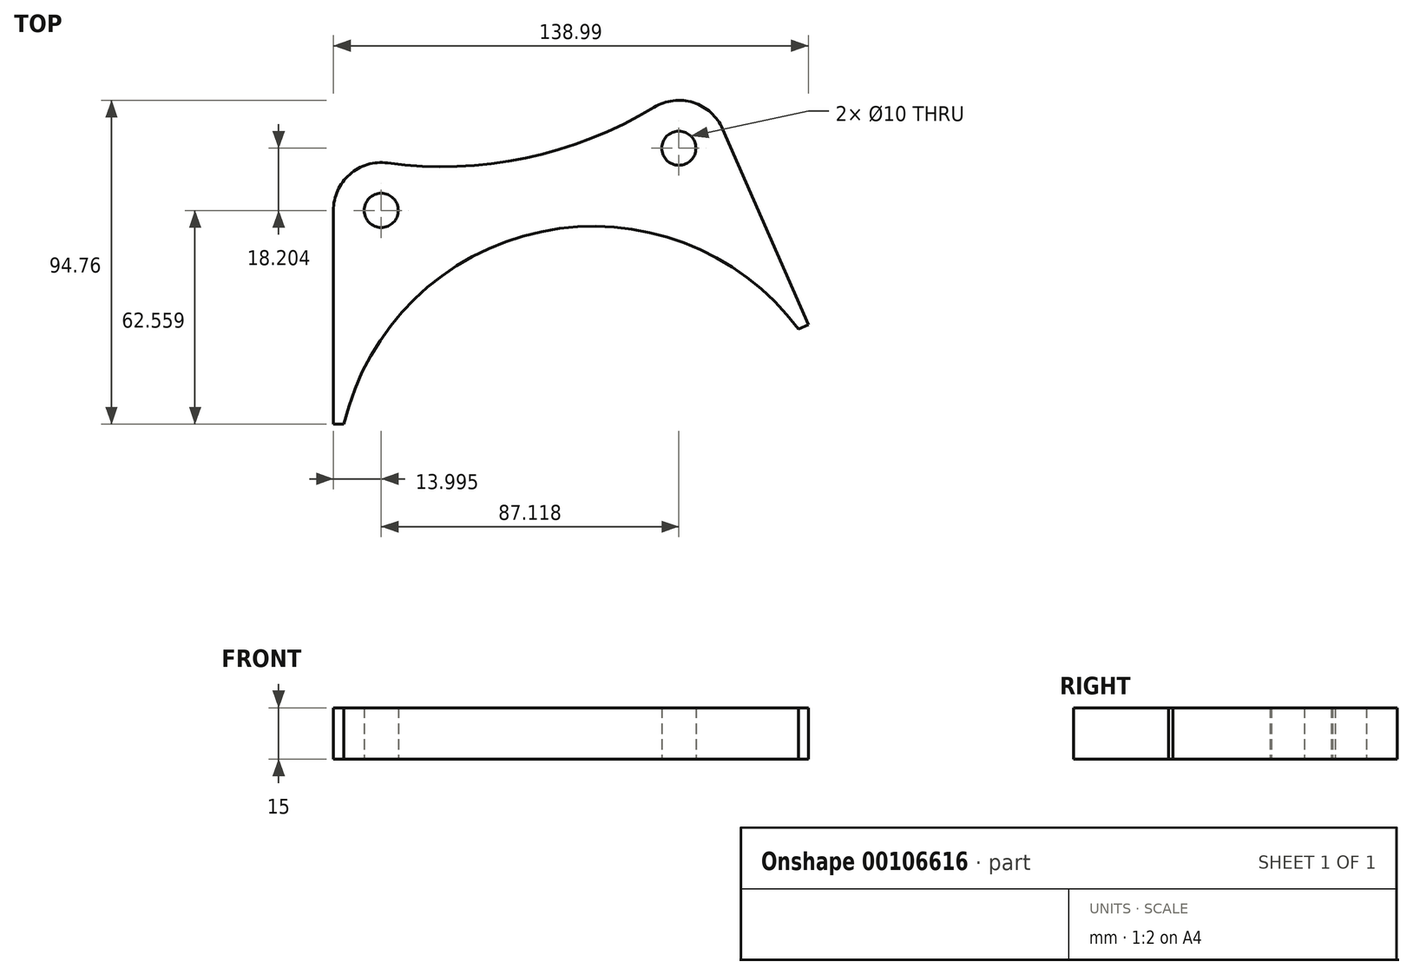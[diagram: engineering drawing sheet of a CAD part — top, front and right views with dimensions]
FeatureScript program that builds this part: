
annotation { "Feature Type Name" : "Feature", "Feature Type Description" : "" }
export const myFeature = defineFeature(function(context is Context, id is Id, definition is map)
    precondition{}
    {
        {
            var Q0;
            Q0=qCreatedBy(makeId("Top.planeOp"),FACE);
            var sketch = newSketch(context, id + "F0", { "sketchPlane" : qUnion([Q0])});
            skArc(sketch, "E0", {"start": v(60.07, 44.9) * mm, "mid": v(-15.34, 73.41) * mm, "end": v(-73.03, 17.1) * mm});
            skCircle(sketch, "E1", {"center": v(0, 0) * mm, "radius": 101 * mm, "construction": true});
            skCircle(sketch, "E2", {"center": v(25.01, 97.85) * mm, "radius": 5 * mm});
            skCircle(sketch, "E3", {"center": v(-62.1, 79.65) * mm, "radius": 5 * mm});
            skArc(sketch, "E4", {"start": v(-60.25, 93.53) * mm, "mid": v(-71.33, 90.18) * mm, "end": v(-76.1, 79.65) * mm});
            skArc(sketch, "E5", {"start": v(37.84, 103.46) * mm, "mid": v(29.25, 111.2) * mm, "end": v(17.76, 109.83) * mm});
            skCircle(sketch, "E6", {"center": v(0, 0) * mm, "radius": 78 * mm, "construction": true});
            skLineSegment(sketch, "E7", {"start": v(-76.1, 79.65) * mm, "end": v(-76.1, 17.1) * mm});
            skLineSegment(sketch, "E8", {"start": v(37.84, 103.46) * mm, "end": v(62.9, 46.14) * mm});
            skArc(sketch, "E9", {"start": v(-60.25, 93.53) * mm, "mid": v(-19.85, 95.01) * mm, "end": v(17.76, 109.83) * mm});
            skLineSegment(sketch, "E10", {"start": v(-76.1, 17.1) * mm, "end": v(-73.03, 17.1) * mm});
            skLineSegment(sketch, "E11", {"start": v(62.9, 46.14) * mm, "end": v(60.07, 44.9) * mm});
            skSolve(sketch);
        }
        {
            var Q0;
            Q0=makeQuery(id+"F0.imprint","IMPRINT",FACE,{"disambiguationData":[TD([[makeQuery(id+"F0.imprint","IMPRINT",EDGE,{"derivedFrom":sQuery(id+"F0.wireOp",EDGE,"E0")}),-1.0]])]});
            extrude(context, id + "F1", {"entities" : qUnion([Q0]), "depth" : 15 * mm});
        }
    });
